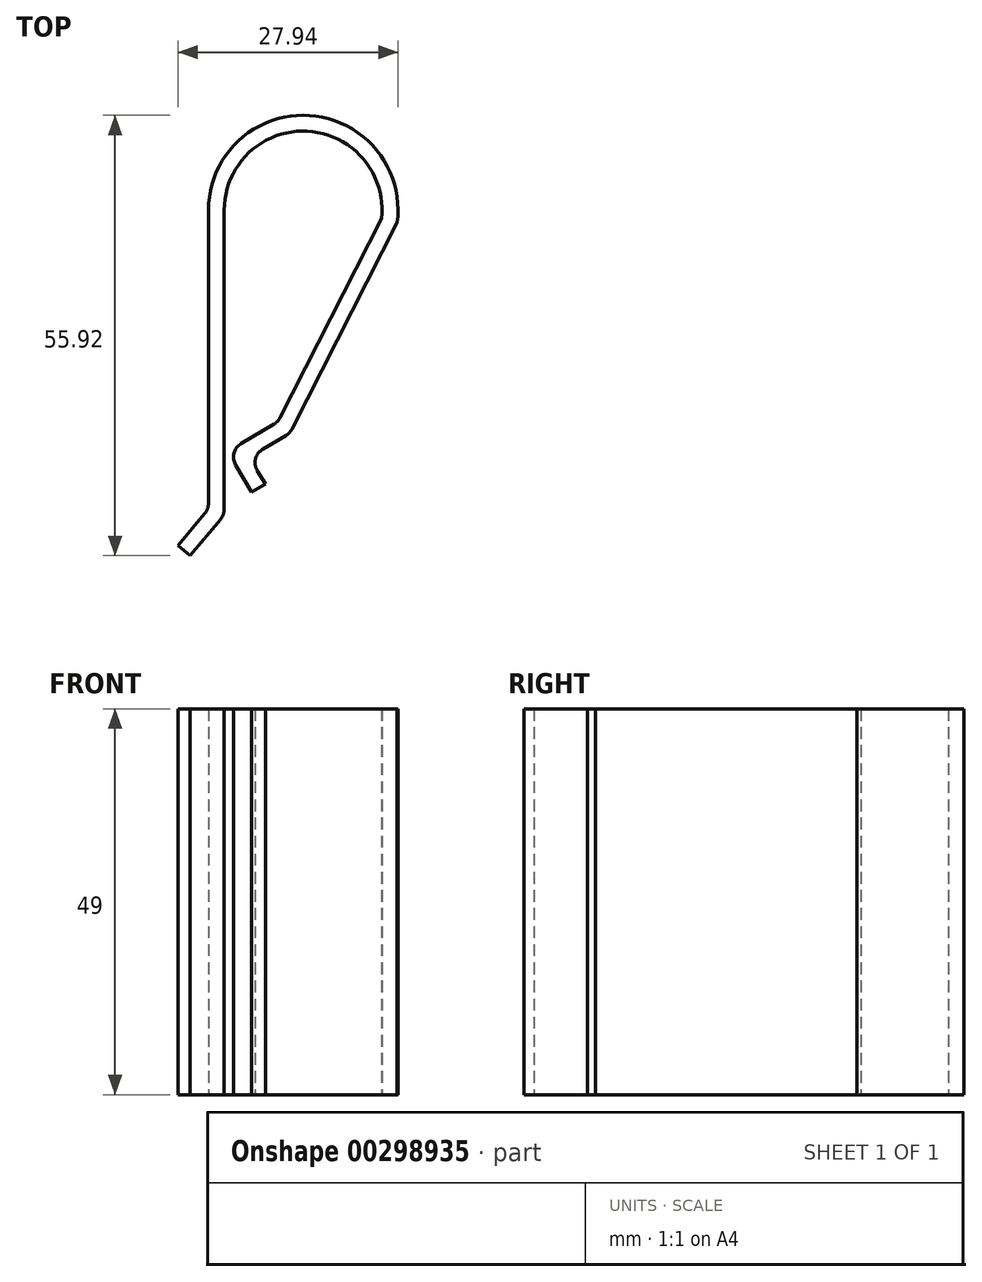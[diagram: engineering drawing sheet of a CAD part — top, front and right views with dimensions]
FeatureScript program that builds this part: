
annotation { "Feature Type Name" : "Feature", "Feature Type Description" : "" }
export const myFeature = defineFeature(function(context is Context, id is Id, definition is map)
    precondition{}
    {
        {
            var Q0;
            Q0=qCreatedBy(makeId("Top.planeOp"),FACE);
            var sketch = newSketch(context, id + "F0", { "sketchPlane" : qUnion([Q0])});
            skLineSegment(sketch, "E0", {"start": v(0, 0) * mm, "end": v(0, 38) * mm});
            skLineSegment(sketch, "E1", {"start": v(-2, 38) * mm, "end": v(-2, 0.73) * mm});
            skLineSegment(sketch, "E2", {"start": v(-2.47, -0.56) * mm, "end": v(-5.86, -4.6) * mm});
            skLineSegment(sketch, "E3", {"start": v(-5.86, -4.6) * mm, "end": v(-4.32, -5.88) * mm});
            skLineSegment(sketch, "E4", {"start": v(-4.32, -5.88) * mm, "end": v(-0.47, -1.29) * mm});
            skLineSegment(sketch, "E5", {"start": v(8.62, 10.2) * mm, "end": v(21.97, 36.4) * mm});
            skLineSegment(sketch, "E6", {"start": v(7.1, 11.62) * mm, "end": v(20, 36.94) * mm});
            skArc(sketch, "E7", {"start": v(20, 36.94) * mm, "mid": v(10.56, 48.01) * mm, "end": v(0, 38) * mm});
            skArc(sketch, "E8", {"start": v(21.97, 36.4) * mm, "mid": v(10.84, 50.01) * mm, "end": v(-2, 38) * mm});
            skLineSegment(sketch, "E9", {"start": v(20, 36.94) * mm, "end": v(16.86, 36.94) * mm, "construction": true});
            skLineSegment(sketch, "E10", {"start": v(1.47, 5.6) * mm, "end": v(3.5, 2.16) * mm});
            skLineSegment(sketch, "E11", {"start": v(3.5, 2.16) * mm, "end": v(5.23, 3.18) * mm});
            skLineSegment(sketch, "E12", {"start": v(5.23, 3.18) * mm, "end": v(4.2, 4.9) * mm});
            skLineSegment(sketch, "E13", {"start": v(4.91, 7.64) * mm, "end": v(7.85, 9.38) * mm});
            skLineSegment(sketch, "E14", {"start": v(2.17, 8.34) * mm, "end": v(6.33, 10.8) * mm});
            skPoint(sketch, "E15.visualSharp", {"position": v(6.83, 11.1) * mm});
            skArc(sketch, "E15.filletArc", {"start": v(6.33, 10.8) * mm, "mid": v(6.77, 11.16) * mm, "end": v(7.1, 11.62) * mm});
            skPoint(sketch, "E16.visualSharp", {"position": v(8.35, 9.68) * mm});
            skArc(sketch, "E16.filletArc", {"start": v(7.85, 9.38) * mm, "mid": v(8.3, 9.73) * mm, "end": v(8.62, 10.2) * mm});
            skPoint(sketch, "E17.visualSharp", {"position": v(3.19, 6.62) * mm});
            skArc(sketch, "E17.filletArc", {"start": v(4.91, 7.64) * mm, "mid": v(4, 6.41) * mm, "end": v(4.2, 4.9) * mm});
            skPoint(sketch, "E18.visualSharp", {"position": v(0.45, 7.32) * mm});
            skArc(sketch, "E18.filletArc", {"start": v(2.17, 8.34) * mm, "mid": v(1.25, 7.12) * mm, "end": v(1.47, 5.6) * mm});
            skPoint(sketch, "E19.visualSharp", {"position": v(0, -0.73) * mm});
            skArc(sketch, "E19.filletArc", {"start": v(-0.47, -1.29) * mm, "mid": v(-0.12, -0.68) * mm, "end": v(0, 0) * mm});
            skArc(sketch, "E20.filletArc", {"start": v(-2.47, -0.56) * mm, "mid": v(-2.12, 0.04) * mm, "end": v(-2, 0.73) * mm});
            skSolve(sketch);
        }
        {
            var Q0;
            Q0 = qSketchRegion(id + "F0", true);
            extrude(context, id + "F1", {"entities" : qUnion([Q0]), "depth" : 49 * mm});
        }
        {
            var Q0;
            Q0=qCreatedBy(makeId("Top.planeOp"),FACE);
            cPlane(context, id + "F2", {"entities" : qUnion([Q0]), "cplaneType" : CPlaneType.OFFSET, "offset" : 4.5 * mm, "width" : 150 * mm, "height" : 150 * mm});
        }
    });
